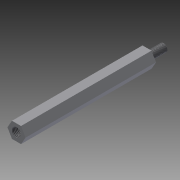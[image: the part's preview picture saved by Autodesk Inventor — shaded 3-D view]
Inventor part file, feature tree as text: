
AUTODESK INVENTOR PART (.ipt)
format: ipt  version: 2015 (Build 190159000, 159)  size: 86,016 bytes
history: native  units: mm
features: extrude x3, sketch x3, thread x2
ambient origin geometry x8: Origin, YZ Plane, XZ Plane, XY Plane, X Axis, Y Axis, Z Axis, Center Point
bodies: Solid1 (feature_tree)
feature tree (8):
  extrude  "Extrusion1"  Depth=50.0mm TaperAngle=0.0deg
  sketch  "Sketch2"  dims[d4=3.5mm d5=3.0mm]
  extrude  "Extrusion2"  Depth=3.0mm
  extrude  "Extrusion3"  Depth=6.0mm TaperAngle=0.0deg
  thread  "Thread1"  [1 undecoded]
  thread  "Thread2"  [1 undecoded]
  sketch  "Sketch1"  dims[d1=6.0mm d2=50.0mm d3=0.0mm]
  sketch  "Sketch3"  dims[d6=6.31mm d7=0.0mm d8=6.0mm d9=0.0mm d10=10.0mm d11=0.0mm d12=10.0mm d13=0.0mm]
note: 2 required parameter values undecoded (feature->parameter linkage not recoverable at this tier; creation-order binding heuristic only, values carry confidence <= 0.55)
